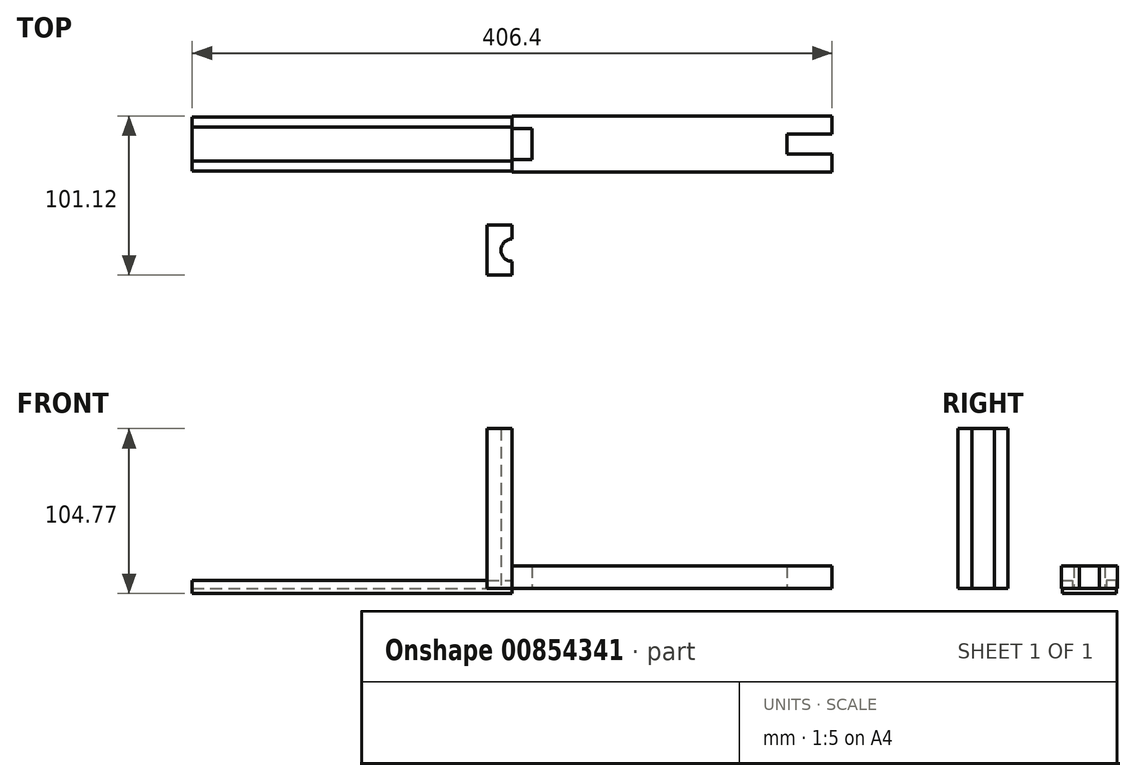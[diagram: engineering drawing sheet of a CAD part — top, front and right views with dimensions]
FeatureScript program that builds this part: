
annotation { "Feature Type Name" : "Feature", "Feature Type Description" : "" }
export const myFeature = defineFeature(function(context is Context, id is Id, definition is map)
    precondition{}
    {
        {
            var Q0;
            Q0=qCreatedBy(makeId("Top.planeOp"),FACE);
            var sketch = newSketch(context, id + "F0", { "sketchPlane" : qUnion([Q0])});
            skLineSegment(sketch, "E0.bottom", {"start": v(-203.2, 10.8) * mm, "end": v(0, 10.8) * mm});
            skLineSegment(sketch, "E0.top", {"start": v(-203.2, -10.8) * mm, "end": v(0, -10.8) * mm});
            skLineSegment(sketch, "E0.left", {"start": v(-203.2, 10.8) * mm, "end": v(-203.2, -10.8) * mm});
            skLineSegment(sketch, "E0.right", {"start": v(0, 10.8) * mm, "end": v(0, -10.8) * mm});
            skLineSegment(sketch, "E1", {"start": v(-203.2, 10.8) * mm, "end": v(-203.2, 17.14) * mm});
            skLineSegment(sketch, "E2", {"start": v(-203.2, 17.14) * mm, "end": v(0, 17.14) * mm});
            skLineSegment(sketch, "E3", {"start": v(0, 17.14) * mm, "end": v(0, 10.8) * mm});
            skLineSegment(sketch, "E4.MirrorCS", {"start": v(-203.2, -17.14) * mm, "end": v(0, -17.14) * mm});
            skLineSegment(sketch, "E5.MirrorCS", {"start": v(0, -17.14) * mm, "end": v(0, -10.8) * mm});
            skLineSegment(sketch, "E6.MirrorCS", {"start": v(-203.2, -10.8) * mm, "end": v(-203.2, -17.14) * mm});
            skLineSegment(sketch, "E7.bottom", {"start": v(0, 17.78) * mm, "end": v(203.2, 17.78) * mm});
            skLineSegment(sketch, "E7.top", {"start": v(0, -17.78) * mm, "end": v(203.2, -17.78) * mm});
            skLineSegment(sketch, "E7.left", {"start": v(0, 17.78) * mm, "end": v(0, -17.78) * mm});
            skLineSegment(sketch, "E7.right", {"start": v(203.2, 17.78) * mm, "end": v(203.2, -17.78) * mm});
            skLineSegment(sketch, "E8.bottom", {"start": v(0, 9.78) * mm, "end": v(12.7, 9.78) * mm});
            skLineSegment(sketch, "E8.top", {"start": v(0, -9.78) * mm, "end": v(12.7, -9.78) * mm});
            skLineSegment(sketch, "E8.left", {"start": v(0, 9.78) * mm, "end": v(0, -9.78) * mm});
            skLineSegment(sketch, "E8.right", {"start": v(12.7, 9.78) * mm, "end": v(12.7, -9.78) * mm});
            skLineSegment(sketch, "E9.bottom", {"start": v(174.62, 6.35) * mm, "end": v(203.2, 6.35) * mm});
            skLineSegment(sketch, "E9.top", {"start": v(174.62, -6.35) * mm, "end": v(203.2, -6.35) * mm});
            skLineSegment(sketch, "E9.left", {"start": v(174.62, 6.35) * mm, "end": v(174.62, -6.35) * mm});
            skLineSegment(sketch, "E9.right", {"start": v(203.2, 6.35) * mm, "end": v(203.2, -6.35) * mm});
            skPoint(sketch, "E10", {"position": v(203.2, 0) * mm});
            skLineSegment(sketch, "E11.bottom", {"start": v(-15.87, -51.59) * mm, "end": v(15.87, -51.59) * mm});
            skLineSegment(sketch, "E11.top", {"start": v(-15.88, -83.34) * mm, "end": v(15.88, -83.34) * mm});
            skLineSegment(sketch, "E11.left", {"start": v(-15.87, -51.59) * mm, "end": v(-15.88, -83.34) * mm});
            skLineSegment(sketch, "E11.right", {"start": v(15.88, -51.59) * mm, "end": v(15.87, -83.34) * mm});
            skCircle(sketch, "E12", {"center": v(0, -67.46) * mm, "radius": 7.11 * mm});
            skPoint(sketch, "E13", {"position": v(-15.88, -67.46) * mm});
            skPoint(sketch, "E14", {"position": v(0, -51.59) * mm});
            skLineSegment(sketch, "E15", {"start": v(0, -51.59) * mm, "end": v(0, -83.34) * mm});
            skSolve(sketch);
        }
        {
            var Q0;
            Q0=makeQuery(id+"F0.imprint","IMPRINT",FACE,{"disambiguationData":[TD([[makeQuery(id+"F0.imprint","IMPRINT",EDGE,{"derivedFrom":sQuery(id+"F0.wireOp",EDGE,"E0.top")}),-1.0]])]});
            var Q1;
            Q1=makeQuery(id+"F0.imprint","IMPRINT",FACE,{"disambiguationData":[TD([[makeQuery(id+"F0.imprint","IMPRINT",EDGE,{"derivedFrom":sQuery(id+"F0.wireOp",EDGE,"E0.bottom")}),-1.0]])]});
            var Q2;
            Q2=makeQuery(id+"F0.imprint","IMPRINT",FACE,{"disambiguationData":[TD([[makeQuery(id+"F0.imprint","IMPRINT",EDGE,{"derivedFrom":sQuery(id+"F0.wireOp",EDGE,"E0.bottom")}),1.0]])]});
            extrude(context, id + "F1", {"entities" : qUnion([Q0, Q1, Q2]), "oppositeDirection" : true, "depth" : 3.17 * mm, "offsetDistance" : 25.4 * mm});
        }
        {
            var Q0;
            Q0=makeQuery(id+"F0.imprint","IMPRINT",FACE,{"disambiguationData":[TD([[makeQuery(id+"F0.imprint","IMPRINT",EDGE,{"derivedFrom":sQuery(id+"F0.wireOp",EDGE,"E0.bottom")}),1.0]])]});
            var Q1;
            Q1=makeQuery(id+"F0.imprint","IMPRINT",FACE,{"disambiguationData":[TD([[makeQuery(id+"F0.imprint","IMPRINT",EDGE,{"derivedFrom":sQuery(id+"F0.wireOp",EDGE,"E0.top")}),-1.0]])]});
            extrude(context, id + "F2", {"entities" : qUnion([Q0, Q1]), "operationType" : NewBodyOperationType.ADD, "depth" : 5.08 * mm, "offsetDistance" : 25.4 * mm});
        }
        {
            var Q0;
            {var subQ4=sQuery(id+"F0.wireOp",EDGE,"E7.bottom");Q0=makeQuery(id+"F0.imprint","IMPRINT",FACE,{"disambiguationData":[TD([[makeQuery(id+"F0.imprint","IMPRINT",EDGE,{"derivedFrom":subQ4}),-1.0]])]});}
            extrude(context, id + "F3", {"entities" : qUnion([Q0]), "depth" : 14.29 * mm, "offsetDistance" : 25.4 * mm});
        }
        {
            var Q0;
            {var subQ4=sQuery(id+"F0.wireOp",EDGE,"E11.left");Q0=makeQuery(id+"F0.imprint","IMPRINT",FACE,{"disambiguationData":[TD([[makeQuery(id+"F0.imprint","IMPRINT",EDGE,{"derivedFrom":subQ4}),1.0]])]});}
            extrude(context, id + "F4", {"entities" : qUnion([Q0]), "depth" : 101.6 * mm, "offsetDistance" : 25.4 * mm});
        }
    });
